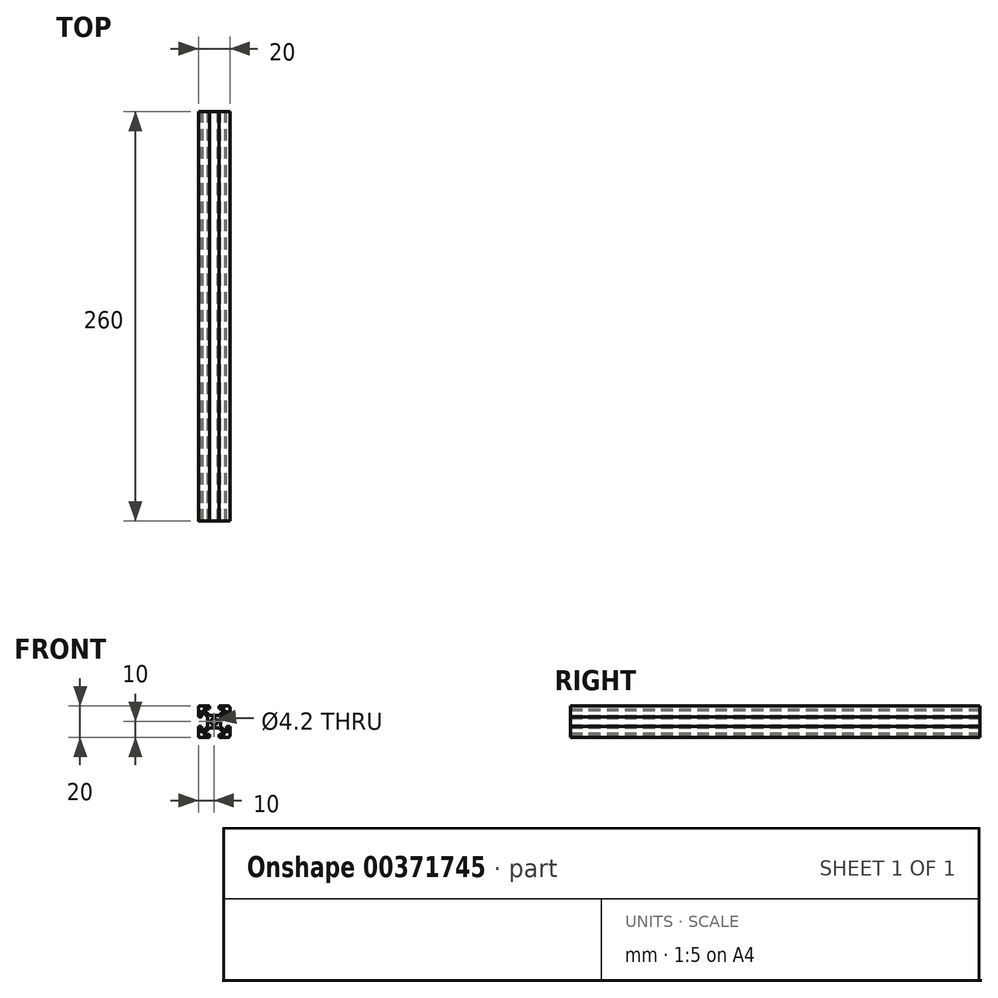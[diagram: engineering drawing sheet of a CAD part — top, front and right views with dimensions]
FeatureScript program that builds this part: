
annotation { "Feature Type Name" : "Feature", "Feature Type Description" : "" }
export const myFeature = defineFeature(function(context is Context, id is Id, definition is map)
    precondition{}
    {
        {
            var Q0;
            Q0=qCreatedBy(makeId("Front.planeOp"),FACE);
            var sketch = newSketch(context, id + "F0", { "sketchPlane" : qUnion([Q0])});
            skLineSegment(sketch, "E0.top", {"start": v(-9, -10) * mm, "end": v(-3, -10) * mm});
            skLineSegment(sketch, "E0.left", {"start": v(-10, 9) * mm, "end": v(-10, 3.08) * mm});
            skLineSegment(sketch, "E0.right", {"start": v(10, 9) * mm, "end": v(10, 3.08) * mm});
            skPoint(sketch, "E0.middle", {"position": v(0, 0) * mm});
            skArc(sketch, "E1.filletArc", {"start": v(-9, 10) * mm, "mid": v(-9.7, 9.7) * mm, "end": v(-10, 9) * mm});
            skArc(sketch, "E2.filletArc", {"start": v(10, 9) * mm, "mid": v(9.7, 9.7) * mm, "end": v(9, 10) * mm});
            skPoint(sketch, "E3.visualSharp", {"position": v(10, -10) * mm});
            skArc(sketch, "E3.filletArc", {"start": v(9, -10) * mm, "mid": v(9.7, -9.7) * mm, "end": v(10, -9) * mm});
            skArc(sketch, "E4.filletArc", {"start": v(-10, -9) * mm, "mid": v(-9.7, -9.7) * mm, "end": v(-9, -10) * mm});
            skCircle(sketch, "E5", {"center": v(0, 0) * mm, "radius": 2.1 * mm});
            skLineSegment(sketch, "E6.bottom", {"start": v(-3, 4) * mm, "end": v(3, 4) * mm});
            skLineSegment(sketch, "E6.top", {"start": v(-3, -4) * mm, "end": v(3, -4) * mm});
            skLineSegment(sketch, "E6.left", {"start": v(-4, 3) * mm, "end": v(-4, -3) * mm});
            skLineSegment(sketch, "E6.right", {"start": v(4, 3) * mm, "end": v(4, -3) * mm});
            skLineSegment(sketch, "E7", {"start": v(-4, 3) * mm, "end": v(-8, 7) * mm});
            skLineSegment(sketch, "E8", {"start": v(-7, 8) * mm, "end": v(-3, 4) * mm});
            skLineSegment(sketch, "E9", {"start": v(3, 4) * mm, "end": v(7, 8) * mm});
            skLineSegment(sketch, "E10", {"start": v(4, 3) * mm, "end": v(8, 7) * mm});
            skLineSegment(sketch, "E11", {"start": v(4, -3) * mm, "end": v(8, -7) * mm});
            skLineSegment(sketch, "E12", {"start": v(3, -4) * mm, "end": v(7, -8) * mm});
            skLineSegment(sketch, "E13", {"start": v(-3, -4) * mm, "end": v(-7, -8) * mm});
            skLineSegment(sketch, "E14", {"start": v(-8, -7) * mm, "end": v(-4, -3) * mm});
            skLineSegment(sketch, "E15.bottom", {"start": v(-7, 8) * mm, "end": v(-3, 8) * mm});
            skLineSegment(sketch, "E15.top", {"start": v(-7, -8) * mm, "end": v(-3, -8) * mm});
            skLineSegment(sketch, "E15.left", {"start": v(-8, 7) * mm, "end": v(-8, 3.18) * mm});
            skLineSegment(sketch, "E15.right", {"start": v(8, 7) * mm, "end": v(8, 3.08) * mm});
            skLineSegment(sketch, "E16", {"start": v(-3, -8) * mm, "end": v(-3, -10) * mm});
            skLineSegment(sketch, "E17", {"start": v(3, -8) * mm, "end": v(3, -10) * mm});
            skLineSegment(sketch, "E18", {"start": v(8, 3.08) * mm, "end": v(10, 3.08) * mm});
            skLineSegment(sketch, "E19", {"start": v(8, -3) * mm, "end": v(10, -3) * mm});
            skLineSegment(sketch, "E20", {"start": v(-3, 10) * mm, "end": v(-3, 8) * mm});
            skLineSegment(sketch, "E21", {"start": v(3, 10) * mm, "end": v(3, 8) * mm});
            skLineSegment(sketch, "E22", {"start": v(-10, 3.08) * mm, "end": v(-8.1, 3.08) * mm});
            skLineSegment(sketch, "E23", {"start": v(-10, -3) * mm, "end": v(-8, -3) * mm});
            skLineSegment(sketch, "E24.trimOffspring", {"start": v(-8, -3) * mm, "end": v(-8, -7) * mm});
            skLineSegment(sketch, "E25.trimOffspring", {"start": v(-10, -3) * mm, "end": v(-10, -9) * mm});
            skLineSegment(sketch, "E26.trimOffspring", {"start": v(3, 10) * mm, "end": v(9, 10) * mm});
            skLineSegment(sketch, "E27.trimOffspring", {"start": v(3, 8) * mm, "end": v(7, 8) * mm});
            skLineSegment(sketch, "E28", {"start": v(-9, 10) * mm, "end": v(-3, 10) * mm});
            skLineSegment(sketch, "E29.trimOffspring", {"start": v(10, -3) * mm, "end": v(10, -9) * mm});
            skLineSegment(sketch, "E30.trimOffspring", {"start": v(8, -3) * mm, "end": v(8, -7) * mm});
            skLineSegment(sketch, "E31.trimOffspring", {"start": v(3, -10) * mm, "end": v(9, -10) * mm});
            skLineSegment(sketch, "E32.trimOffspring", {"start": v(3, -8) * mm, "end": v(7, -8) * mm});
            skPoint(sketch, "E33.visualSharp", {"position": v(-8, 3.08) * mm});
            skArc(sketch, "E33.filletArc", {"start": v(-8.1, 3.08) * mm, "mid": v(-8.03, 3.1) * mm, "end": v(-8, 3.18) * mm});
            skSolve(sketch);
        }
        {
            assignVariable(context, id + "F1", {"name" : "x", "anyValue" : 260});
        }
        {
            var Q0;
            Q0=makeQuery(id+"F0.imprint","IMPRINT",FACE,{"disambiguationData":[TD([[makeQuery(id+"F0.imprint","IMPRINT",EDGE,{"derivedFrom":sQuery(id+"F0.wireOp",EDGE,"E0.top")}),1.0]])]});
            extrude(context, id + "F2", {"entities" : qUnion([Q0]), "depth" : (getVariable(context, 'x')) * mm});
        }
    });
